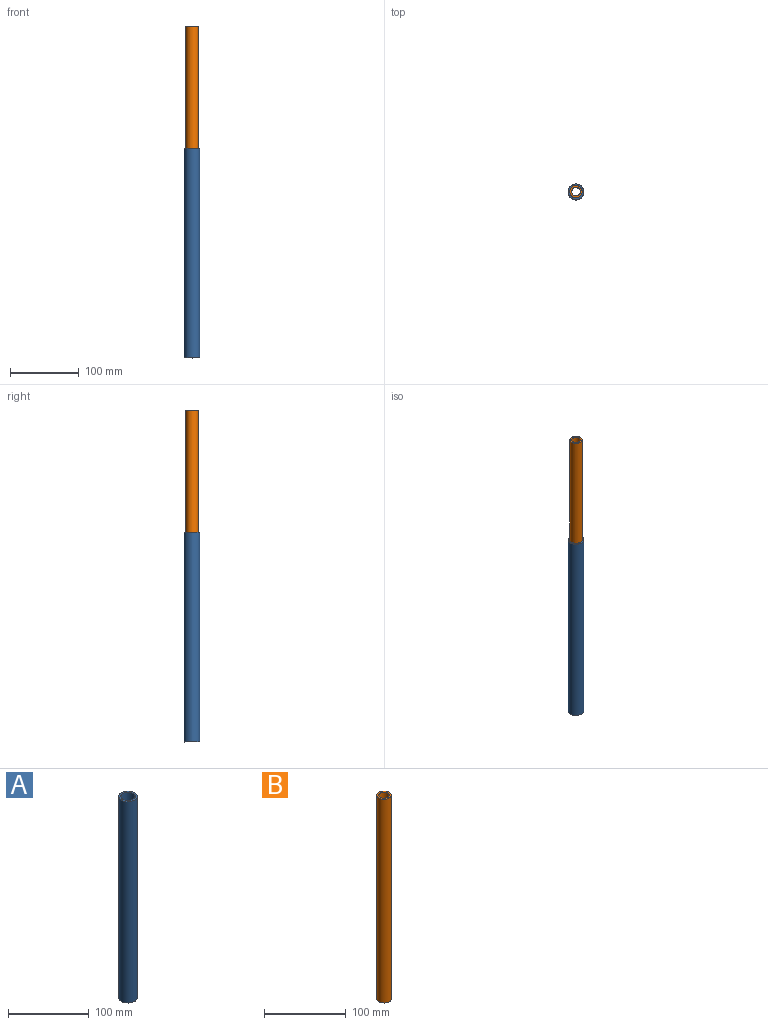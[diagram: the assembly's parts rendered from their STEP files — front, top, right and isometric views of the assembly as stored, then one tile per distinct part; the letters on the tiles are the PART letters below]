
ASSEMBLY  parts=2 mates=1
PART A: 4 faces, bbox 22.9x22.9x304.8 mm
  f0: cylinder r=8.89mm len=304.8mm, axis (0,0,1), area 17025.4mm2, adj f2,f3
  f1: cylinder r=11.43mm len=304.8mm, axis (0,0,1), area 21889.8mm2, adj f2,f3
  f2: plane 22.86x22.86mm, normal (0,0,-1), area 162.1mm2, adj f0,f1
  f3: plane 22.86x22.86mm, normal (0,0,1), area 162.1mm2, adj f0,f1
PART B: 4 faces, bbox 17.8x17.8x304.8 mm
  f0: cylinder r=6.35mm len=304.8mm, axis (0,0,-1), area 12161mm2, adj f2,f3
  f1: cylinder r=8.89mm len=304.8mm, axis (0,0,-1), area 17025.4mm2, adj f2,f3
  f2: plane 17.78x17.78mm, normal (0,0,1), area 121.6mm2, adj f0,f1
  f3: plane 17.78x17.78mm, normal (0,0,-1), area 121.6mm2, adj f0,f1
PLACE A rot(axis=(-0.75,0.07,0.65),0deg) t=(-196.59,281.58,293.36)mm
PLACE B rot(axis=(1,0,0),180deg) t=(-196.59,281.58,471.16)mm
MATE slider B.f1 <-> A.f1  axis (0,0,1) through (-196.59,281.58,318.76)mm
